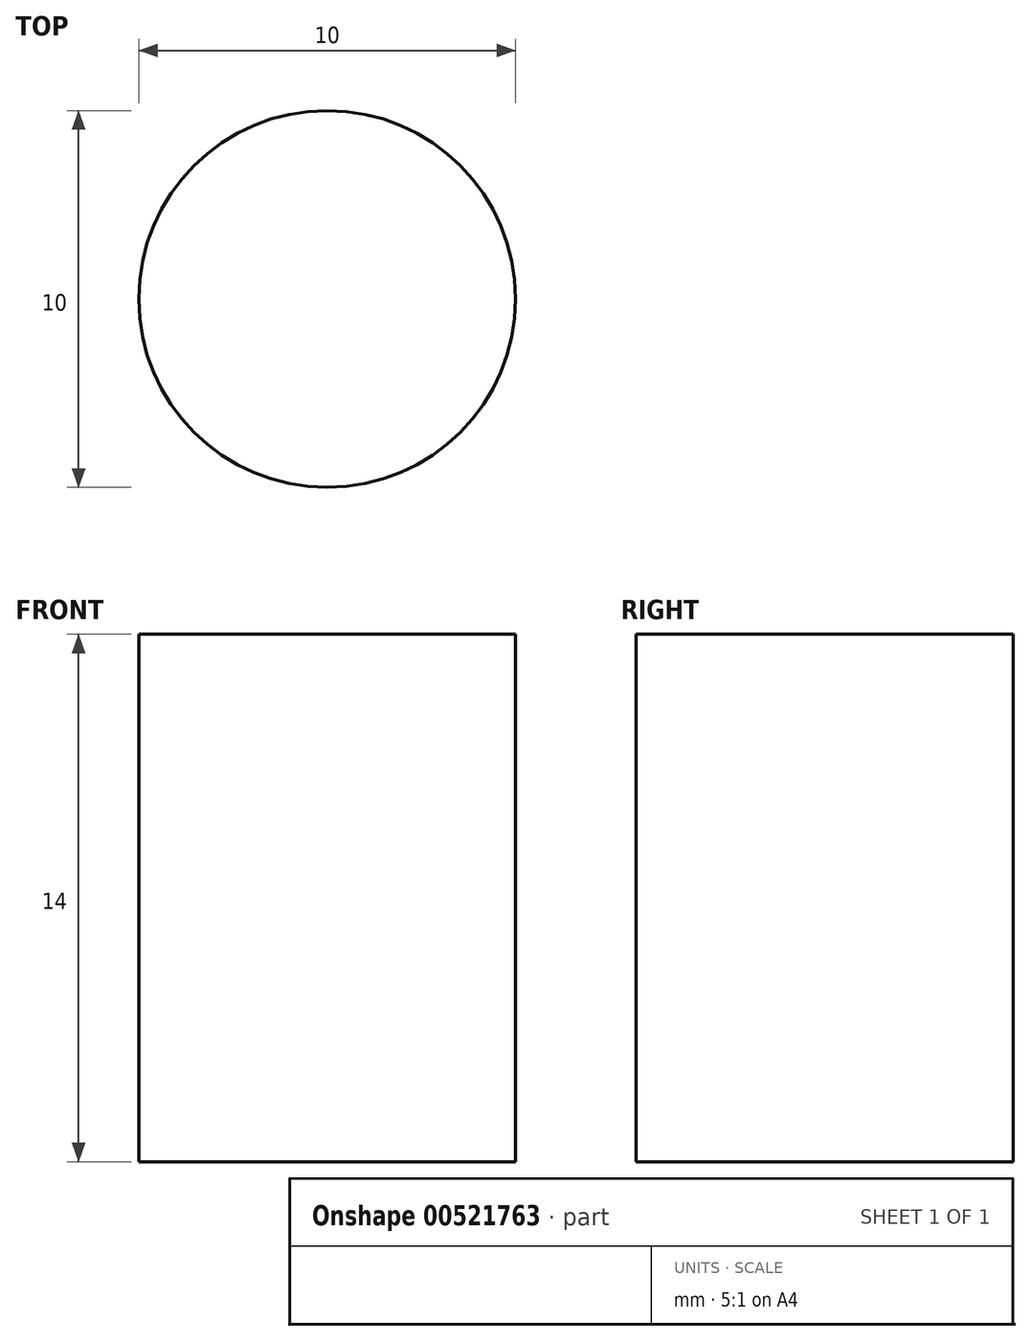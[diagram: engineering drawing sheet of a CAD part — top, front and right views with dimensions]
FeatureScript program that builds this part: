
annotation { "Feature Type Name" : "Feature", "Feature Type Description" : "" }
export const myFeature = defineFeature(function(context is Context, id is Id, definition is map)
    precondition{}
    {
        {
            var Q0;
            Q0=qCreatedBy(makeId("Top.planeOp"),FACE);
            var sketch = newSketch(context, id + "F0", { "sketchPlane" : qUnion([Q0])});
            skCircle(sketch, "E0", {"center": v(0, 0) * mm, "radius": 5 * mm});
            skSolve(sketch);
        }
        {
            var Q0;
            Q0=makeQuery(id+"F0.imprint","IMPRINT",FACE,{"disambiguationData":[TD([[makeQuery(id+"F0.imprint","IMPRINT",EDGE,{"derivedFrom":sQuery(id+"F0.wireOp",EDGE,"E0")}),1.0]])]});
            extrude(context, id + "F1", {"entities" : qUnion([Q0]), "depth" : 14 * mm, "offsetDistance" : 25 * mm});
        }
    });
